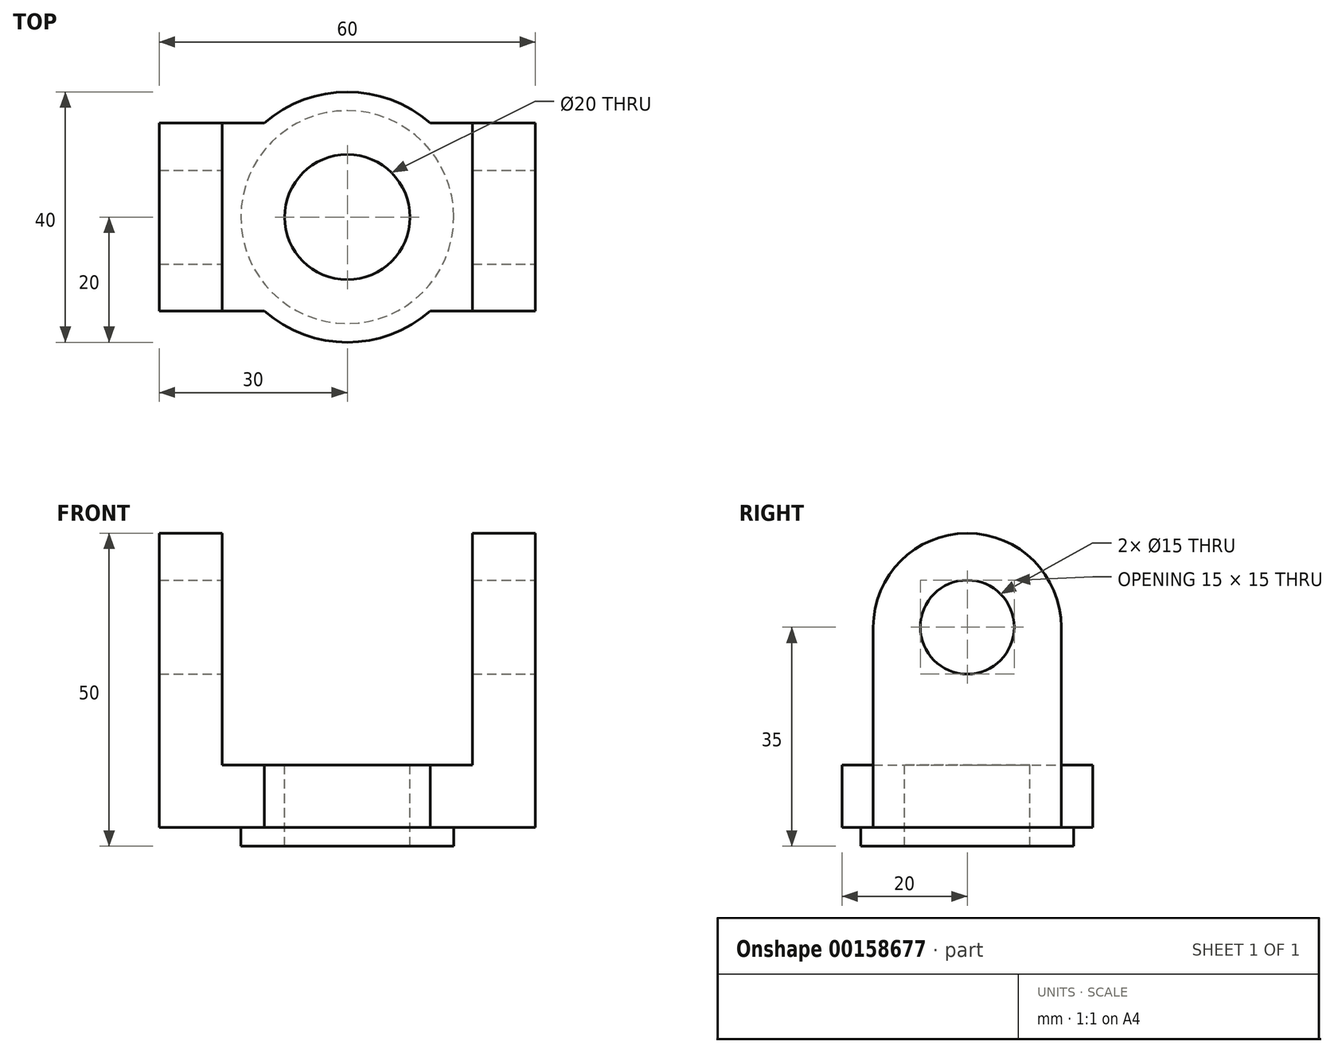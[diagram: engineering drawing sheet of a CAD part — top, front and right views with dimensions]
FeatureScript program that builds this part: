
annotation { "Feature Type Name" : "Feature", "Feature Type Description" : "" }
export const myFeature = defineFeature(function(context is Context, id is Id, definition is map)
    precondition{}
    {
        {
            var Q0;
            Q0=qCreatedBy(makeId("Front.planeOp"),FACE);
            var sketch = newSketch(context, id + "F0", { "sketchPlane" : qUnion([Q0])});
            skLineSegment(sketch, "E0.bottom", {"start": v(0, 0) * mm, "end": v(60, 0) * mm});
            skLineSegment(sketch, "E0.top", {"start": v(0, 10) * mm, "end": v(60, 10) * mm});
            skLineSegment(sketch, "E0.left", {"start": v(0, 0) * mm, "end": v(0, 10) * mm});
            skLineSegment(sketch, "E0.right", {"start": v(60, 0) * mm, "end": v(60, 10) * mm});
            skSolve(sketch);
        }
        {
            var Q0;
            Q0 = qSketchRegion(id + "F0", true);
            extrude(context, id + "F1", {"entities" : qUnion([Q0]), "oppositeDirection" : true, "depth" : 30 * mm});
        }
        {
            var Q0;
            Q0=makeQuery(id+"F1.opExtrude","SWEPT_FACE",FACE,{"disambiguationData":[OSD([sQuery(id+"F0.wireOp",EDGE,"E0.top")])]});
            var sketch = newSketch(context, id + "F2", { "sketchPlane" : qUnion([Q0])});
            skCircle(sketch, "E1", {"center": v(30, 15) * mm, "radius": 20 * mm});
            skSolve(sketch);
        }
        {
            var Q0;
            Q0 = qSketchRegion(id + "F2", true);
            extrude(context, id + "F3", {"entities" : qUnion([Q0]), "operationType" : NewBodyOperationType.ADD, "oppositeDirection" : true, "depth" : 10 * mm});
        }
        {
            var Q0;
            Q0=makeQuery(id+"F3.boolean.opBoolean","MERGE",FACE,{"derivedFrom":[makeQuery(id+"F1.opExtrude","SWEPT_FACE",FACE,{"disambiguationData":[OSD([sQuery(id+"F0.wireOp",EDGE,"E0.bottom")])]}),makeQuery(id+"F3.opExtrude","CAP_FACE",FACE,{"disambiguationData":[OSD([sQuery(id+"F2.wireOp",EDGE,"E1")])],"isStart":false})]});
            var sketch = newSketch(context, id + "F4", { "sketchPlane" : qUnion([Q0])});
            skCircle(sketch, "E2", {"center": v(30, -15) * mm, "radius": 17 * mm});
            skSolve(sketch);
        }
        {
            var Q0;
            Q0 = qSketchRegion(id + "F4", true);
            extrude(context, id + "F5", {"entities" : qUnion([Q0]), "operationType" : NewBodyOperationType.ADD, "depth" : 3 * mm});
        }
        {
            var Q0;
            {var subQ1=sQuery(id+"F0.wireOp",EDGE,"E0.top");var subQ6=makeQuery(id+"F1.opExtrude","SWEPT_EDGE",EDGE,{"disambiguationData":[OSD([subQ1,sQuery(id+"F0.wireOp",EDGE,"E0.right")])]});Q0=makeQuery(id+"F2.imprint","IMPRINT",FACE,{"disambiguationData":[TD([[makeQuery(id+"F2.imprint","IMPRINT",EDGE,{"derivedFrom":subQ6}),-1.0]])]});}
            var sketch = newSketch(context, id + "F6", { "sketchPlane" : qUnion([Q0])});
            skLineSegment(sketch, "E3.bottom", {"start": v(60, 0) * mm, "end": v(50, 0) * mm});
            skLineSegment(sketch, "E3.top", {"start": v(60, 30) * mm, "end": v(50, 30) * mm});
            skLineSegment(sketch, "E3.left", {"start": v(60, 0) * mm, "end": v(60, 30) * mm});
            skLineSegment(sketch, "E3.right", {"start": v(50, 0) * mm, "end": v(50, 30) * mm});
            skLineSegment(sketch, "E4.bottom", {"start": v(0, 0) * mm, "end": v(10, 0) * mm});
            skLineSegment(sketch, "E4.top", {"start": v(0, 30) * mm, "end": v(10, 30) * mm});
            skLineSegment(sketch, "E4.left", {"start": v(0, 0) * mm, "end": v(0, 30) * mm});
            skLineSegment(sketch, "E4.right", {"start": v(10, 0) * mm, "end": v(10, 30) * mm});
            skSolve(sketch);
        }
        {
            var Q0;
            Q0 = qSketchRegion(id + "F6", true);
            extrude(context, id + "F7", {"entities" : qUnion([Q0]), "operationType" : NewBodyOperationType.ADD, "depth" : 40 * mm});
        }
        {
            var Q0;
            Q0=makeQuery(id+"F7.boolean.opBoolean","MERGE",FACE,{"derivedFrom":[makeQuery(id+"F1.opExtrude","SWEPT_FACE",FACE,{"disambiguationData":[OSD([sQuery(id+"F0.wireOp",EDGE,"E0.right")])]}),makeQuery(id+"F7.opExtrude","SWEPT_FACE",FACE,{"disambiguationData":[OSD([sQuery(id+"F6.wireOp",EDGE,"E3.left")])]})]});
            var sketch = newSketch(context, id + "F8", { "sketchPlane" : qUnion([Q0])});
            skCircle(sketch, "E5", {"center": v(15, 32) * mm, "radius": 7.5 * mm});
            skSolve(sketch);
        }
        {
            var Q0;
            Q0 = qSketchRegion(id + "F8", true);
            extrude(context, id + "F9", {"entities" : qUnion([Q0]), "operationType" : NewBodyOperationType.REMOVE, "endBound" : BoundingType.THROUGH_ALL, "oppositeDirection" : true, "depth" : 25 * mm});
        }
        {
            var Q0;
            Q0=makeQuery(id+"F7.boolean.opBoolean","MERGE",FACE,{"derivedFrom":[makeQuery(id+"F1.opExtrude","SWEPT_FACE",FACE,{"disambiguationData":[OSD([sQuery(id+"F0.wireOp",EDGE,"E0.right")])]}),makeQuery(id+"F7.opExtrude","SWEPT_FACE",FACE,{"disambiguationData":[OSD([sQuery(id+"F6.wireOp",EDGE,"E3.left")])]})]});
            var sketch = newSketch(context, id + "F10", { "sketchPlane" : qUnion([Q0])});
            skArc(sketch, "E6", {"start": v(30, 32) * mm, "mid": v(15, 47) * mm, "end": v(0, 32) * mm});
            skLineSegment(sketch, "E7", {"start": v(0, 32) * mm, "end": v(0, 50) * mm});
            skLineSegment(sketch, "E8", {"start": v(0, 50) * mm, "end": v(30, 50) * mm});
            skLineSegment(sketch, "E9", {"start": v(30, 50) * mm, "end": v(30, 32) * mm});
            skSolve(sketch);
        }
        {
            var Q0;
            Q0 = qSketchRegion(id + "F10", true);
            extrude(context, id + "F11", {"entities" : qUnion([Q0]), "operationType" : NewBodyOperationType.REMOVE, "endBound" : BoundingType.THROUGH_ALL, "oppositeDirection" : true, "depth" : 25 * mm});
        }
        {
            var Q0;
            {var subQ0=sQuery(id+"F2.wireOp",EDGE,"E1");var subQ1=sQuery(id+"F0.wireOp",EDGE,"E0.top");var subQ2=makeQuery(id+"F1.opExtrude","CAP_EDGE",EDGE,{"disambiguationData":[OSD([subQ1])],"isStart":false});var subQ3=makeQuery(id+"F2.imprint","INTERSECT",VERTEX,{"disambiguationData":[OD(0.0)],"derivedFrom":[subQ2,subQ0]});Q0=makeQuery(id+"F2.imprint","IMPRINT",FACE,{"disambiguationData":[TD([[makeQuery(id+"F2.imprint","IMPRINT",EDGE,{"disambiguationData":[TD([[subQ3,-1.0]])],"derivedFrom":subQ0}),1.0]])]});}
            var sketch = newSketch(context, id + "F12", { "sketchPlane" : qUnion([Q0])});
            skCircle(sketch, "E10", {"center": v(30, 15) * mm, "radius": 10 * mm});
            skSolve(sketch);
        }
        {
            var Q0;
            Q0 = qSketchRegion(id + "F12", true);
            extrude(context, id + "F13", {"entities" : qUnion([Q0]), "operationType" : NewBodyOperationType.REMOVE, "endBound" : BoundingType.THROUGH_ALL, "oppositeDirection" : true, "depth" : 25 * mm});
        }
    });
